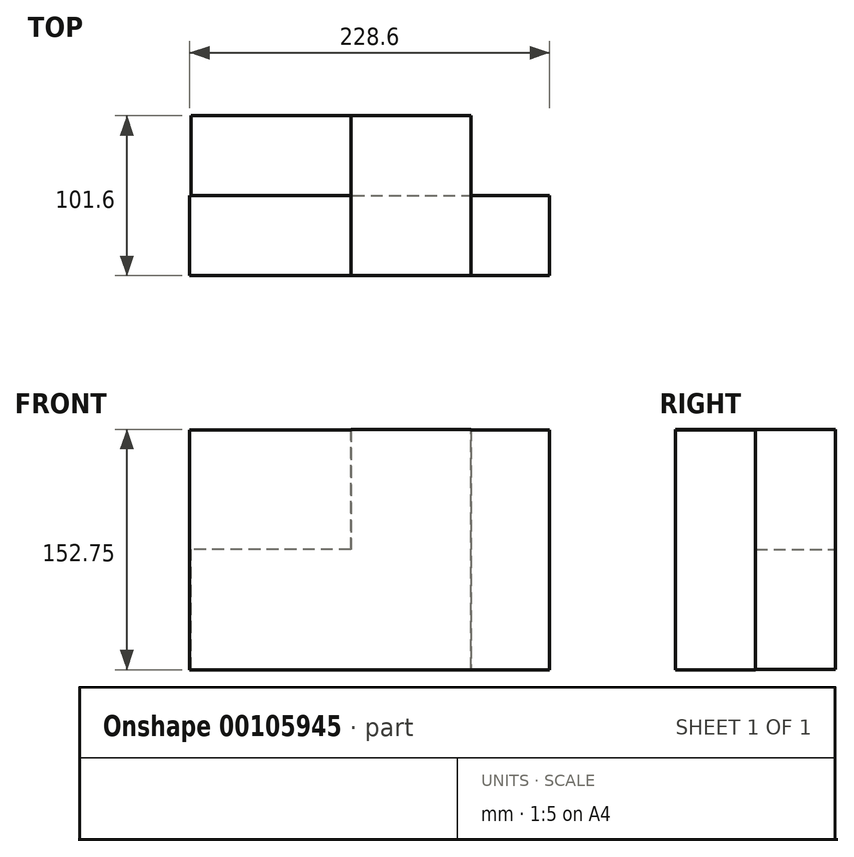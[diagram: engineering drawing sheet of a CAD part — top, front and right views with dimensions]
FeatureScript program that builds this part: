
annotation { "Feature Type Name" : "Feature", "Feature Type Description" : "" }
export const myFeature = defineFeature(function(context is Context, id is Id, definition is map)
    precondition{}
    {
        {
            var Q0;
            Q0=qCreatedBy(makeId("Front.planeOp"),FACE);
            var sketch = newSketch(context, id + "F0", { "sketchPlane" : qUnion([Q0])});
            skLineSegment(sketch, "E0", {"start": v(-117.98, 68.41) * mm, "end": v(-117.98, -83.88) * mm});
            skLineSegment(sketch, "E1", {"start": v(-117.98, -83.88) * mm, "end": v(110.62, -83.88) * mm});
            skLineSegment(sketch, "E2", {"start": v(110.62, -83.88) * mm, "end": v(110.62, 68.41) * mm});
            skLineSegment(sketch, "E3", {"start": v(110.62, 68.41) * mm, "end": v(-117.98, 68.41) * mm});
            skSolve(sketch);
        }
        {
            var Q0;
            Q0 = qSketchRegion(id + "F0", true);
            extrude(context, id + "F1", {"entities" : qUnion([Q0]), "depth" : 50.8 * mm});
        }
        {
            var Q0;
            Q0=qCreatedBy(makeId("Front.planeOp"),FACE);
            var sketch = newSketch(context, id + "F2", { "sketchPlane" : qUnion([Q0])});
            skLineSegment(sketch, "E4", {"start": v(-117.28, -7.33) * mm, "end": v(-15.68, -7.33) * mm});
            skLineSegment(sketch, "E5", {"start": v(-15.68, -7.33) * mm, "end": v(-15.68, 68.87) * mm});
            skLineSegment(sketch, "E6", {"start": v(-15.68, 68.87) * mm, "end": v(60.52, 68.87) * mm});
            skLineSegment(sketch, "E7", {"start": v(-117.28, -7.33) * mm, "end": v(-117.28, -83.53) * mm});
            skLineSegment(sketch, "E8", {"start": v(60.52, 68.87) * mm, "end": v(60.52, -83.53) * mm});
            skLineSegment(sketch, "E9", {"start": v(-117.28, -83.53) * mm, "end": v(60.52, -83.53) * mm});
            skSolve(sketch);
        }
        {
            var Q0;
            Q0 = qSketchRegion(id + "F2", true);
            extrude(context, id + "F3", {"entities" : qUnion([Q0]), "operationType" : NewBodyOperationType.ADD, "endBound" : BoundingType.SYMMETRIC, "depth" : 101.6 * mm});
        }
    });
